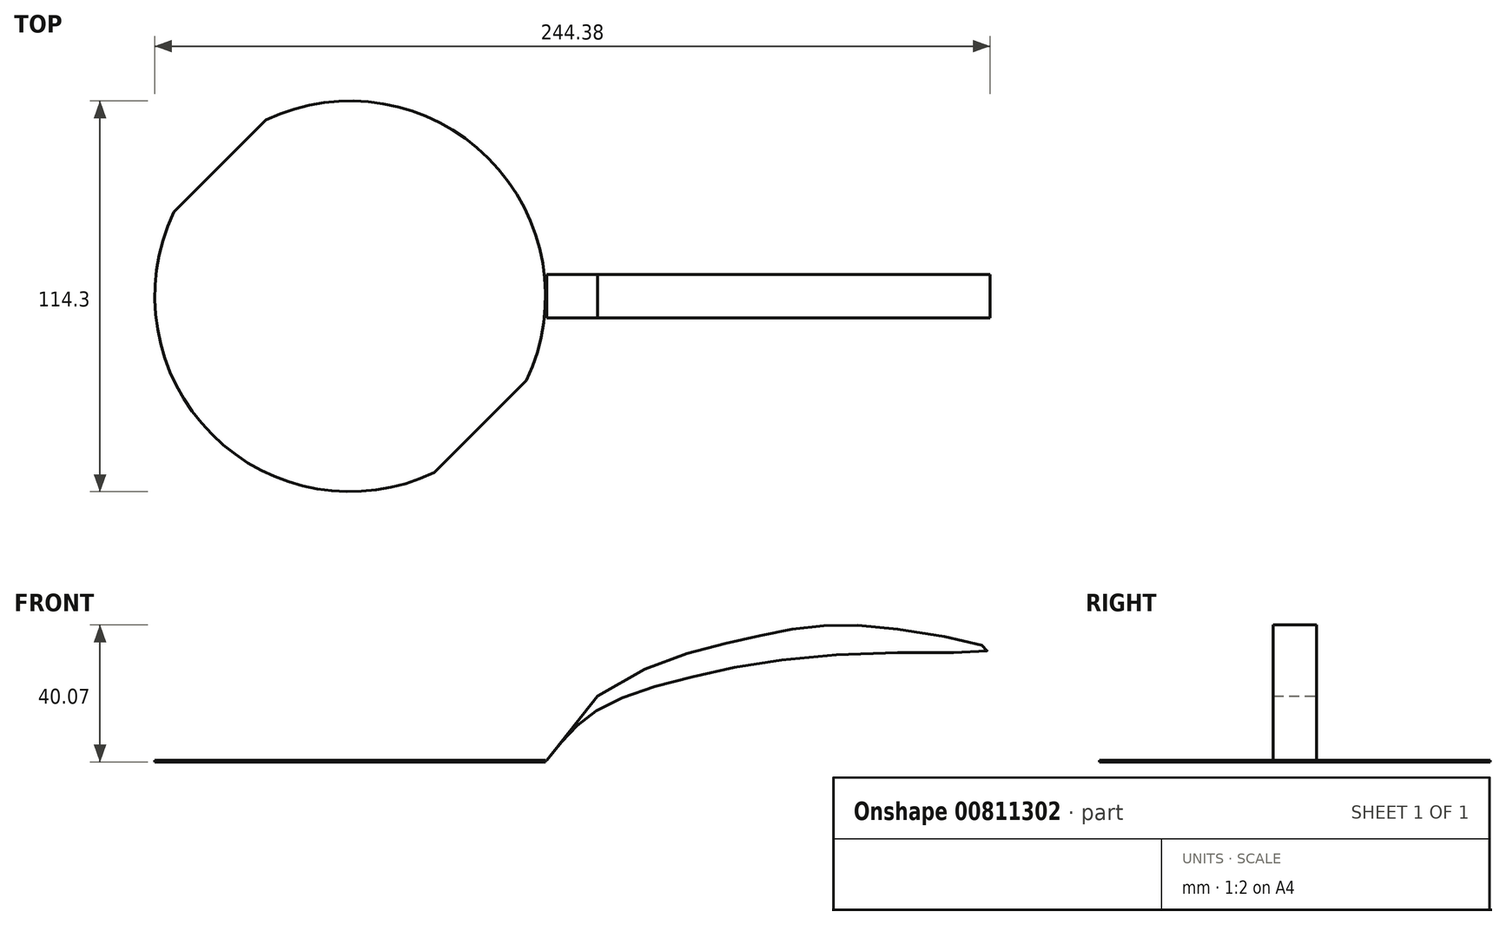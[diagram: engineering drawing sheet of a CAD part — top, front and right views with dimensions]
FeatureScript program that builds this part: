
annotation { "Feature Type Name" : "Feature", "Feature Type Description" : "" }
export const myFeature = defineFeature(function(context is Context, id is Id, definition is map)
    precondition{}
    {
        {
            var Q0;
            Q0=qCreatedBy(makeId("Top.planeOp"),FACE);
            var sketch = newSketch(context, id + "F0", { "sketchPlane" : qUnion([Q0])});
            skCircle(sketch, "E0", {"center": v(0, 0) * mm, "radius": 57.15 * mm});
            skLineSegment(sketch, "E1", {"start": v(40.41, 40.41) * mm, "end": v(-40.41, -40.41) * mm});
            skLineSegment(sketch, "E2.1.0.0", {"start": v(46.26, 33.56) * mm, "end": v(-33.56, -46.26) * mm});
            skLineSegment(sketch, "E2.2.0.0", {"start": v(51.06, 25.66) * mm, "end": v(-25.66, -51.06) * mm});
            skLineSegment(sketch, "E2.3.0.0", {"start": v(54.69, 16.59) * mm, "end": v(-16.59, -54.69) * mm});
            skLineSegment(sketch, "E2.4.0.0", {"start": v(56.83, 6.03) * mm, "end": v(-6.03, -56.83) * mm});
            skLineSegment(sketch, "E2.5.0.0", {"start": v(56.75, -6.75) * mm, "end": v(6.75, -56.75) * mm});
            skLineSegment(sketch, "E2.6.0.0", {"start": v(51.57, -24.63) * mm, "end": v(24.63, -51.57) * mm});
            skLineSegment(sketch, "E3.1.0.0", {"start": v(33.56, 46.26) * mm, "end": v(-46.26, -33.56) * mm});
            skLineSegment(sketch, "E3.2.0.0", {"start": v(25.66, 51.06) * mm, "end": v(-51.06, -25.66) * mm});
            skLineSegment(sketch, "E3.3.0.0", {"start": v(16.59, 54.69) * mm, "end": v(-54.69, -16.59) * mm});
            skLineSegment(sketch, "E3.4.0.0", {"start": v(6.03, 56.83) * mm, "end": v(-56.83, -6.03) * mm});
            skLineSegment(sketch, "E3.5.0.0", {"start": v(-6.75, 56.75) * mm, "end": v(-56.75, 6.75) * mm});
            skLineSegment(sketch, "E3.6.0.0", {"start": v(-24.63, 51.57) * mm, "end": v(-51.57, 24.63) * mm});
            skSolve(sketch);
        }
        {
            var Q0;
            Q0=qCreatedBy(makeId("Top.planeOp"),FACE);
            cPlane(context, id + "F1", {"entities" : qUnion([Q0]), "cplaneType" : CPlaneType.OFFSET, "offset" : 19.05 * mm, "width" : 152.4 * mm, "height" : 152.4 * mm});
        }
        {
            var Q0;
            Q0=qCreatedBy(id+"F1.planeOp",FACE);
            var sketch = newSketch(context, id + "F2", { "sketchPlane" : qUnion([Q0])});
            skCircle(sketch, "E4", {"center": v(0, 0) * mm, "radius": 73.03 * mm});
            skSolve(sketch);
        }
        {
            var Q0;
            Q0=makeQuery(id+"F2.imprint","IMPRINT",FACE,{"disambiguationData":[TD([[makeQuery(id+"F2.imprint","IMPRINT",EDGE,{"derivedFrom":sQuery(id+"F2.wireOp",EDGE,"E4")}),1.0]])]});
            var Q1;
            Q1=makeQuery(id+"F0.imprint","IMPRINT",FACE,{"disambiguationData":[TD([[makeQuery(id+"F0.imprint","IMPRINT",EDGE,{"derivedFrom":sQuery(id+"F0.wireOp",EDGE,"E0")}),1.0]])]});
            var Q2;
            Q2=sQuery(id+"F2.wireOp",EDGE,"E4");
            var Q3;
            Q3=sQuery(id+"F0.wireOp",EDGE,"E0");
            loft(context, id + "F3", {"bodyType" : ToolBodyType.SURFACE, "sheetProfilesArray" : [{ "sheetProfileEntities" : qUnion([Q0]) }, { "sheetProfileEntities" : qUnion([Q1]) }], "wireProfilesArray" : [{ "wireProfileEntities" : qUnion([Q2]) }, { "wireProfileEntities" : qUnion([Q3]) }]});
        }
        {
            var Q0;
            Q0=makeQuery(id+"F0.imprint","IMPRINT",FACE,{"disambiguationData":[TD([[makeQuery(id+"F0.imprint","IMPRINT",EDGE,{"derivedFrom":sQuery(id+"F0.wireOp",EDGE,"E0")}),1.0]])]});
            extrude(context, id + "F4", {"entities" : qUnion([Q0]), "oppositeDirection" : true, "depth" : 0.5 * mm, "offsetDistance" : 25.4 * mm});
        }
        {
            var Q0;
            Q0=qCreatedBy(makeId("Front.planeOp"),FACE);
            var sketch = newSketch(context, id + "F5", { "sketchPlane" : qUnion([Q0])});
            skLineSegment(sketch, "E5", {"start": v(0, 0) * mm, "end": v(57.46, 0) * mm});
            skFitSpline(sketch, "E6", {"points": [v(57.46, 0) * mm, v(64.65, 8.36) * mm, v(74.53, 15.96) * mm, v(97.63, 23.8) * mm, v(146.06, 31.08) * mm, v(187.23, 32.48) * mm, v(161.65, 38.18) * mm, v(134.37, 39) * mm, v(111.85, 34.56) * mm, v(72.4, 18.83) * mm], "startDerivative": vector(108.06, 128.07) * mm, "endDerivative": vector(-333.23, -228.17) * mm});
            skLineSegment(sketch, "E7", {"start": v(72.4, 18.83) * mm, "end": v(57.46, 0) * mm});
            skSolve(sketch);
        }
        {
            var Q0;
            Q0=makeQuery(id+"F5.imprint","IMPRINT",FACE,{"disambiguationData":[TD([[makeQuery(id+"F5.imprint","IMPRINT",EDGE,{"derivedFrom":sQuery(id+"F5.wireOp",EDGE,"E6")}),1.0]])]});
            extrude(context, id + "F6", {"entities" : qUnion([Q0]), "endBound" : BoundingType.SYMMETRIC, "depth" : 12.7 * mm, "offsetDistance" : 25.4 * mm});
        }
        {
            var Q0;
            Q0=sQuery(id+"F0.wireOp",EDGE,"E3.6.0.0");
            var Q1;
            Q1=sQuery(id+"F0.wireOp",EDGE,"E3.4.0.0");
            var Q2;
            Q2=sQuery(id+"F0.wireOp",EDGE,"E2.3.0.0");
            var Q3;
            Q3=sQuery(id+"F0.wireOp",EDGE,"E3.3.0.0");
            var Q4;
            Q4=sQuery(id+"F0.wireOp",EDGE,"E3.2.0.0");
            var Q5;
            Q5=sQuery(id+"F0.wireOp",EDGE,"E3.1.0.0");
            var Q6;
            Q6=sQuery(id+"F0.wireOp",EDGE,"E2.6.0.0");
            var Q7;
            Q7=sQuery(id+"F0.wireOp",EDGE,"E2.5.0.0");
            var Q8;
            Q8=sQuery(id+"F0.wireOp",EDGE,"E2.2.0.0");
            var Q9;
            Q9=sQuery(id+"F0.wireOp",EDGE,"E2.1.0.0");
            var Q10;
            Q10=sQuery(id+"F0.wireOp",EDGE,"E1");
            var Q11;
            Q11=sQuery(id+"F0.wireOp",EDGE,"E3.5.0.0");
            var Q12;
            Q12=sQuery(id+"F0.wireOp",EDGE,"E2.4.0.0");
            extrude(context, id + "F7", {"bodyType" : ToolBodyType.SURFACE, "surfaceEntities" : qUnion([Q0, Q1, Q2, Q3, Q4, Q5, Q6, Q7, Q8, Q9, Q10, Q11, Q12]), "depth" : 0.5 * mm, "offsetDistance" : 25.4 * mm});
        }
    });
